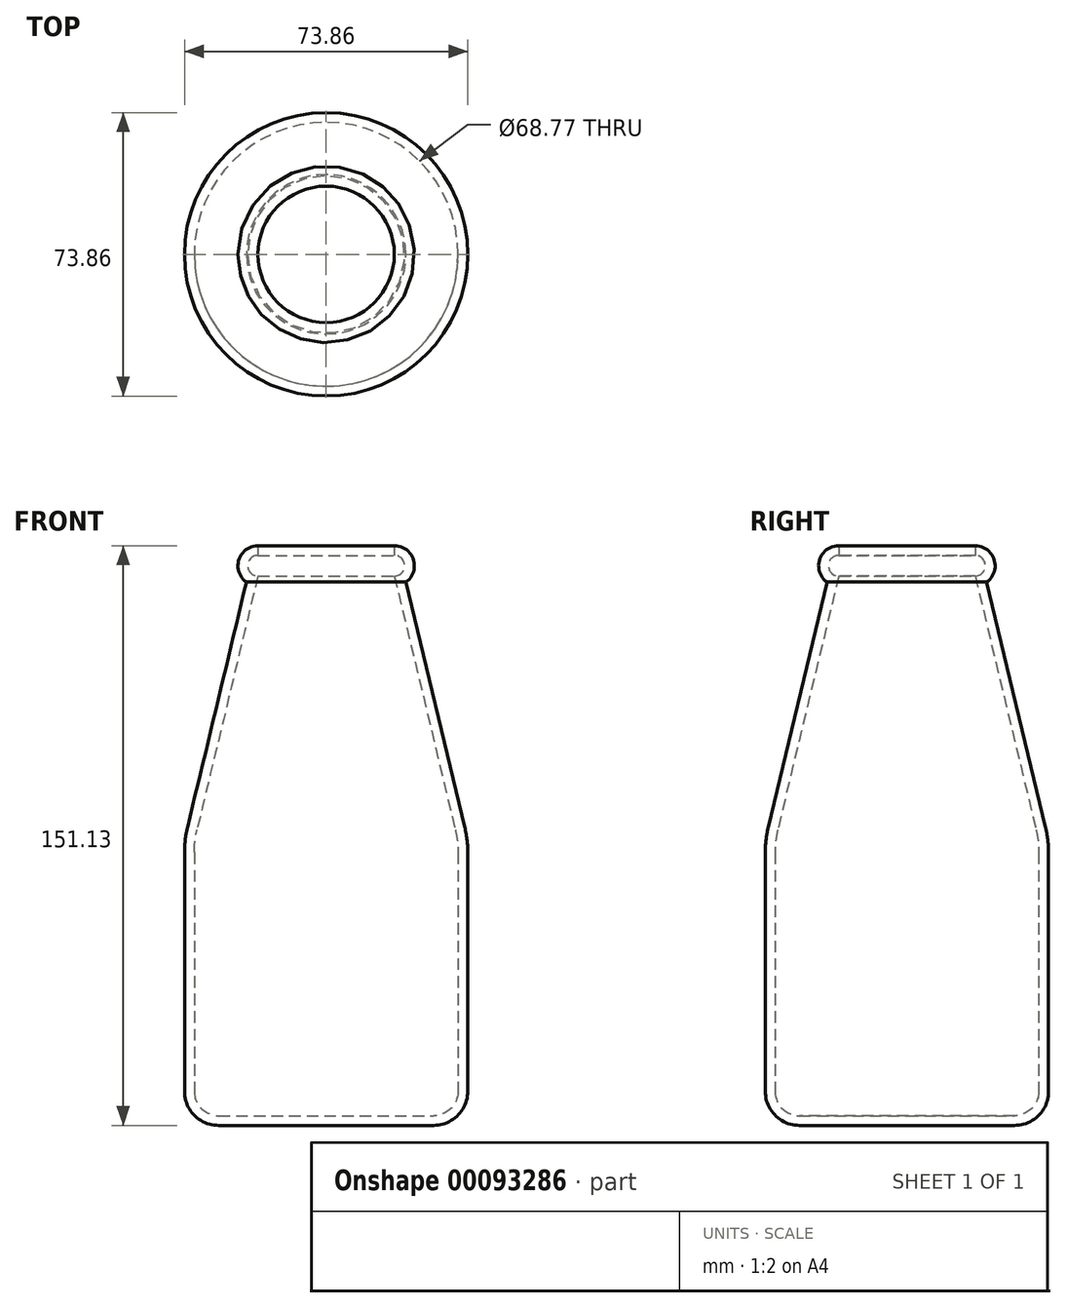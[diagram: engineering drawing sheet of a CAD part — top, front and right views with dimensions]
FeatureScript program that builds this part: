
annotation { "Feature Type Name" : "Feature", "Feature Type Description" : "" }
export const myFeature = defineFeature(function(context is Context, id is Id, definition is map)
    precondition{}
    {
        {
            var Q0;
            Q0=qCreatedBy(makeId("Front.planeOp"),FACE);
            var sketch = newSketch(context, id + "F0", { "sketchPlane" : qUnion([Q0])});
            skLineSegment(sketch, "E0", {"start": v(0, -71.61) * mm, "end": v(0, 74.44) * mm});
            skLineSegment(sketch, "E1", {"start": v(0, -71.61) * mm, "end": v(34.39, -71.61) * mm});
            skLineSegment(sketch, "E2", {"start": v(34.39, -71.61) * mm, "end": v(34.39, 0) * mm});
            skArc(sketch, "E3", {"start": v(17.78, 69.07) * mm, "mid": v(20.47, 71.75) * mm, "end": v(17.78, 74.44) * mm});
            skLineSegment(sketch, "E4", {"start": v(0, 74.44) * mm, "end": v(17.78, 74.44) * mm});
            skLineSegment(sketch, "E5", {"start": v(17.78, 69.07) * mm, "end": v(34.39, 0) * mm});
            skSolve(sketch);
        }
        {
            var Q0;
            Q0 = qSketchRegion(id + "F0", true);
            var Q1;
            Q1=sQuery(id+"F0.wireOp",EDGE,"E0");
            revolve(context, id + "F1", {"entities" : qUnion([Q0]), "axis" : qUnion([Q1]), "revolveType" : RevolveType.FULL});
        }
        {
            var Q0;
            Q0=makeQuery(id+"F1.opRevolve","SWEPT_EDGE",EDGE,{"disambiguationData":[OSD([sQuery(id+"F0.wireOp",EDGE,"E2"),sQuery(id+"F0.wireOp",EDGE,"E5")])]});
            fillet(context, id + "F2", {"entities" : qUnion([Q0]), "radius" : 25.4 * mm, "tangentPropagation" : true, "allowEdgeOverflow" : false});
        }
        {
            var Q0;
            Q0=makeQuery(id+"F1.opRevolve","SWEPT_EDGE",EDGE,{"disambiguationData":[OSD([sQuery(id+"F0.wireOp",EDGE,"E1"),sQuery(id+"F0.wireOp",EDGE,"E2")])]});
            var Q1;
            Q1=makeQuery(id+"F1.opRevolve","SWEPT_FACE",FACE,{"disambiguationData":[OSD([sQuery(id+"F0.wireOp",EDGE,"E2")])]});
            fillet(context, id + "F3", {"entities" : qUnion([Q0, Q1]), "radius" : 6.35 * mm, "tangentPropagation" : true, "allowEdgeOverflow" : false});
        }
        {
            var Q0;
            Q0=makeQuery(id+"F1.opRevolve","SWEPT_FACE",FACE,{"disambiguationData":[OSD([sQuery(id+"F0.wireOp",EDGE,"E4")])]});
            shell(context, id + "F4", {"entities" : qUnion([Q0]), "thickness" : 2.54 * mm, "oppositeDirection" : true});
        }
    });
